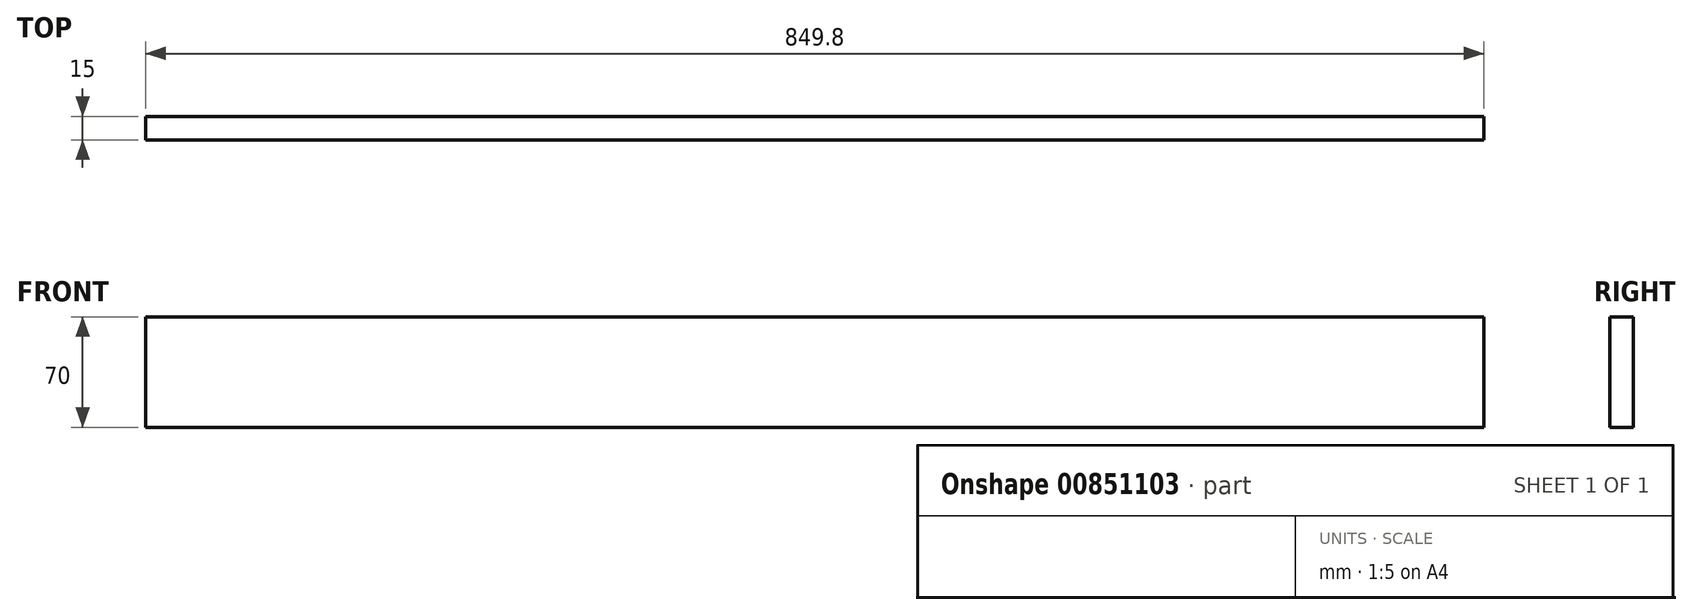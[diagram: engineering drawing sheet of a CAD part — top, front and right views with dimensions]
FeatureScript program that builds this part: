
annotation { "Feature Type Name" : "Feature", "Feature Type Description" : "" }
export const myFeature = defineFeature(function(context is Context, id is Id, definition is map)
    precondition{}
    {
        {
            var Q0;
            Q0=qCreatedBy(makeId("Top.planeOp"),FACE);
            var sketch = newSketch(context, id + "F0", { "sketchPlane" : qUnion([Q0])});
            skLineSegment(sketch, "E0.bottom", {"start": v(-424.9, 7.5) * mm, "end": v(424.9, 7.5) * mm});
            skLineSegment(sketch, "E0.top", {"start": v(-424.9, -7.5) * mm, "end": v(424.9, -7.5) * mm});
            skLineSegment(sketch, "E0.left", {"start": v(-424.9, 7.5) * mm, "end": v(-424.9, -7.5) * mm});
            skLineSegment(sketch, "E0.right", {"start": v(424.9, 7.5) * mm, "end": v(424.9, -7.5) * mm});
            skSolve(sketch);
        }
        {
            var Q0;
            Q0=makeQuery(id+"F0.imprint","IMPRINT",FACE,{"disambiguationData":[TD([[makeQuery(id+"F0.imprint","IMPRINT",EDGE,{"derivedFrom":sQuery(id+"F0.wireOp",EDGE,"E0.bottom")}),-1.0]])]});
            extrude(context, id + "F1", {"entities" : qUnion([Q0]), "endBound" : BoundingType.SYMMETRIC, "depth" : 70 * mm, "offsetDistance" : 25 * mm});
        }
        {
            var Q0;
            Q0=qCreatedBy(makeId("Front.planeOp"),FACE);
            cPlane(context, id + "F2", {"entities" : qUnion([Q0]), "cplaneType" : CPlaneType.OFFSET, "offset" : 25 * mm, "oppositeDirection" : true, "width" : 150 * mm, "height" : 150 * mm});
        }
    });
